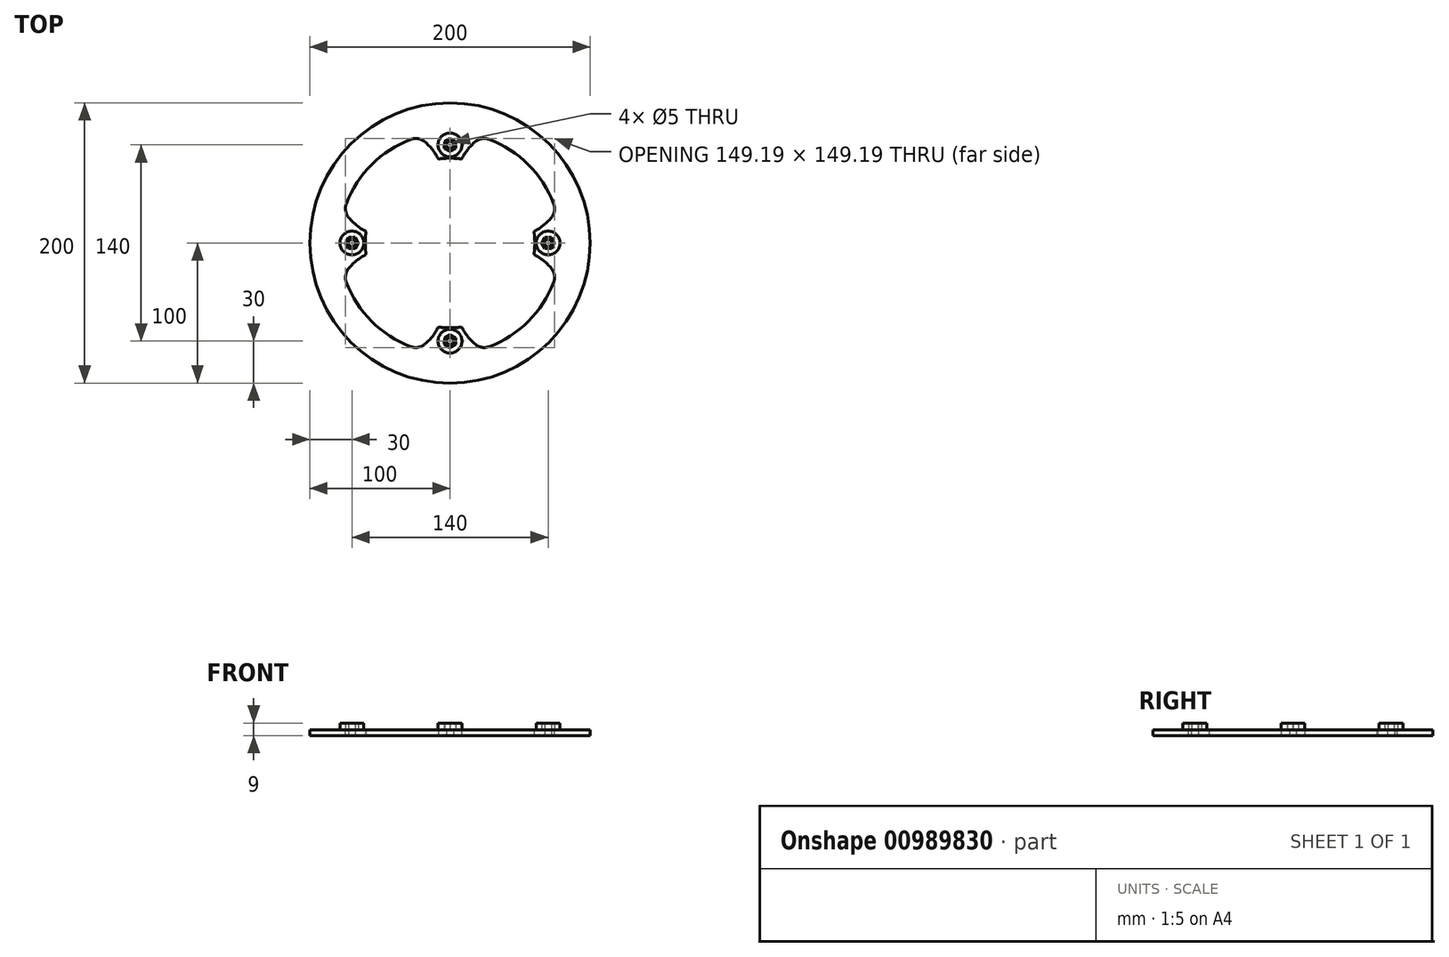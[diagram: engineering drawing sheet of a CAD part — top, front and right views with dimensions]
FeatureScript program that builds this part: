
annotation { "Feature Type Name" : "Feature", "Feature Type Description" : "" }
export const myFeature = defineFeature(function(context is Context, id is Id, definition is map)
    precondition{}
    {
        {
            var Q0;
            Q0=qCreatedBy(makeId("Top.planeOp"),FACE);
            var sketch = newSketch(context, id + "F0", { "sketchPlane" : qUnion([Q0])});
            skCircle(sketch, "E0", {"center": v(0, 0) * mm, "radius": 100 * mm});
            skCircle(sketch, "E1", {"center": v(0, 70) * mm, "radius": 2.5 * mm});
            skCircle(sketch, "E2.1.0", {"center": v(70, 0) * mm, "radius": 2.5 * mm});
            skCircle(sketch, "E2.2.0", {"center": v(0, -70) * mm, "radius": 2.5 * mm});
            skCircle(sketch, "E2.3.0", {"center": v(-70, 0) * mm, "radius": 2.5 * mm});
            skLineSegment(sketch, "E2.anchor1", {"start": v(0, 0) * mm, "end": v(0, 70) * mm, "construction": true});
            skLineSegment(sketch, "E2.anchor2", {"start": v(0, 0) * mm, "end": v(-70, 0) * mm, "construction": true});
            skCircle(sketch, "E3", {"center": v(0, 0) * mm, "radius": 60.5 * mm});
            skLineSegment(sketch, "E4.0", {"start": v(-67.7, -3.72) * mm, "end": v(-72.3, -3.72) * mm});
            skLineSegment(sketch, "E4.1", {"start": v(-72.3, -3.72) * mm, "end": v(-74.62, 0.28) * mm});
            skLineSegment(sketch, "E4.2", {"start": v(-74.62, 0.28) * mm, "end": v(-72.3, 4.28) * mm});
            skLineSegment(sketch, "E4.3", {"start": v(-72.3, 4.28) * mm, "end": v(-67.7, 4.28) * mm});
            skLineSegment(sketch, "E4.4", {"start": v(-67.7, 4.28) * mm, "end": v(-65.38, 0.28) * mm});
            skLineSegment(sketch, "E4.5", {"start": v(-65.38, 0.28) * mm, "end": v(-67.7, -3.72) * mm});
            skPoint(sketch, "E4.0.midPoint", {"position": v(-70, -3.72) * mm});
            skLineSegment(sketch, "E5.1.0", {"start": v(-4.28, -72.3) * mm, "end": v(-4.28, -67.7) * mm});
            skLineSegment(sketch, "E5.1.1", {"start": v(-4.28, -67.7) * mm, "end": v(-0.28, -65.38) * mm});
            skLineSegment(sketch, "E5.1.2", {"start": v(-0.28, -74.62) * mm, "end": v(-4.28, -72.3) * mm});
            skLineSegment(sketch, "E5.1.3", {"start": v(3.72, -72.3) * mm, "end": v(-0.28, -74.62) * mm});
            skLineSegment(sketch, "E5.1.4", {"start": v(3.72, -67.7) * mm, "end": v(3.72, -72.3) * mm});
            skLineSegment(sketch, "E5.1.5", {"start": v(-0.28, -65.38) * mm, "end": v(3.72, -67.7) * mm});
            skLineSegment(sketch, "E5.2.0", {"start": v(72.3, -4.28) * mm, "end": v(67.7, -4.28) * mm});
            skLineSegment(sketch, "E5.2.1", {"start": v(67.7, -4.28) * mm, "end": v(65.38, -0.28) * mm});
            skLineSegment(sketch, "E5.2.2", {"start": v(74.62, -0.28) * mm, "end": v(72.3, -4.28) * mm});
            skLineSegment(sketch, "E5.2.3", {"start": v(72.3, 3.72) * mm, "end": v(74.62, -0.28) * mm});
            skLineSegment(sketch, "E5.2.4", {"start": v(67.7, 3.72) * mm, "end": v(72.3, 3.72) * mm});
            skLineSegment(sketch, "E5.2.5", {"start": v(65.38, -0.28) * mm, "end": v(67.7, 3.72) * mm});
            skLineSegment(sketch, "E5.3.0", {"start": v(4.28, 72.3) * mm, "end": v(4.28, 67.7) * mm});
            skLineSegment(sketch, "E5.3.1", {"start": v(4.28, 67.7) * mm, "end": v(0.28, 65.38) * mm});
            skLineSegment(sketch, "E5.3.2", {"start": v(0.28, 74.62) * mm, "end": v(4.28, 72.3) * mm});
            skLineSegment(sketch, "E5.3.3", {"start": v(-3.72, 72.3) * mm, "end": v(0.28, 74.62) * mm});
            skLineSegment(sketch, "E5.3.4", {"start": v(-3.72, 67.7) * mm, "end": v(-3.72, 72.3) * mm});
            skLineSegment(sketch, "E5.3.5", {"start": v(0.28, 65.38) * mm, "end": v(-3.72, 67.7) * mm});
            skCircle(sketch, "E6", {"center": v(0, 0) * mm, "radius": 79.07 * mm});
            skArc(sketch, "E7", {"start": v(-75.7, 22.83) * mm, "mid": v(-68.85, 14.45) * mm, "end": v(-59.93, 8.3) * mm});
            skArc(sketch, "E8.1.0", {"start": v(-22.83, -75.7) * mm, "mid": v(-14.45, -68.85) * mm, "end": v(-8.3, -59.93) * mm});
            skArc(sketch, "E8.2.0", {"start": v(75.7, -22.83) * mm, "mid": v(68.85, -14.45) * mm, "end": v(59.93, -8.3) * mm});
            skArc(sketch, "E8.3.0", {"start": v(22.83, 75.7) * mm, "mid": v(14.45, 68.85) * mm, "end": v(8.3, 59.93) * mm});
            skArc(sketch, "E9.trimOffspring", {"start": v(-8.3, 59.93) * mm, "mid": v(-14.45, 68.85) * mm, "end": v(-22.83, 75.7) * mm});
            skArc(sketch, "E10.trimOffspring", {"start": v(59.93, 8.3) * mm, "mid": v(68.85, 14.45) * mm, "end": v(75.7, 22.83) * mm});
            skArc(sketch, "E11.trimOffspring", {"start": v(8.3, -59.93) * mm, "mid": v(14.45, -68.85) * mm, "end": v(22.83, -75.7) * mm});
            skArc(sketch, "E12.trimOffspring", {"start": v(-59.93, -8.3) * mm, "mid": v(-68.85, -14.45) * mm, "end": v(-75.7, -22.83) * mm});
            skSolve(sketch);
        }
        {
            var Q0;
            Q0=makeQuery(id+"F0.imprint","IMPRINT",FACE,{"disambiguationData":[TD([[makeQuery(id+"F0.imprint","IMPRINT",EDGE,{"derivedFrom":sQuery(id+"F0.wireOp",EDGE,"E0")}),1.0]])]});
            var Q1;
            Q1=makeQuery(id+"F0.imprint","IMPRINT",FACE,{"disambiguationData":[TD([[makeQuery(id+"F0.imprint","IMPRINT",EDGE,{"derivedFrom":sQuery(id+"F0.wireOp",EDGE,"E2.3.0")}),-1.0]])]});
            var Q2;
            Q2=makeQuery(id+"F0.imprint","IMPRINT",FACE,{"disambiguationData":[TD([[makeQuery(id+"F0.imprint","IMPRINT",EDGE,{"derivedFrom":sQuery(id+"F0.wireOp",EDGE,"E2.2.0")}),-1.0]])]});
            var Q3;
            Q3=makeQuery(id+"F0.imprint","IMPRINT",FACE,{"disambiguationData":[TD([[makeQuery(id+"F0.imprint","IMPRINT",EDGE,{"derivedFrom":sQuery(id+"F0.wireOp",EDGE,"E2.1.0")}),-1.0]])]});
            var Q4;
            Q4=makeQuery(id+"F0.imprint","IMPRINT",FACE,{"disambiguationData":[TD([[makeQuery(id+"F0.imprint","IMPRINT",EDGE,{"derivedFrom":sQuery(id+"F0.wireOp",EDGE,"E1")}),-1.0]])]});
            var Q5;
            Q5=makeQuery(id+"F0.imprint","IMPRINT",FACE,{"disambiguationData":[TD([[makeQuery(id+"F0.imprint","IMPRINT",EDGE,{"derivedFrom":sQuery(id+"F0.wireOp",EDGE,"E5.3.0")}),1.0]])]});
            var Q6;
            Q6=makeQuery(id+"F0.imprint","IMPRINT",FACE,{"disambiguationData":[TD([[makeQuery(id+"F0.imprint","IMPRINT",EDGE,{"derivedFrom":sQuery(id+"F0.wireOp",EDGE,"E4.0")}),1.0]])]});
            var Q7;
            Q7=makeQuery(id+"F0.imprint","IMPRINT",FACE,{"disambiguationData":[TD([[makeQuery(id+"F0.imprint","IMPRINT",EDGE,{"derivedFrom":sQuery(id+"F0.wireOp",EDGE,"E5.2.0")}),1.0]])]});
            var Q8;
            Q8=makeQuery(id+"F0.imprint","IMPRINT",FACE,{"disambiguationData":[TD([[makeQuery(id+"F0.imprint","IMPRINT",EDGE,{"derivedFrom":sQuery(id+"F0.wireOp",EDGE,"E5.1.0")}),1.0]])]});
            extrude(context, id + "F1", {"entities" : qUnion([Q0, Q1, Q2, Q3, Q4, Q5, Q6, Q7, Q8]), "depth" : 4 * mm, "offsetDistance" : 25 * mm});
        }
        {
            var Q0;
            Q0=makeQuery(id+"F1.opExtrude","CAP_FACE",FACE,{"disambiguationData":[OSD([sQuery(id+"F0.wireOp",EDGE,"E0"),sQuery(id+"F0.wireOp",EDGE,"E1"),sQuery(id+"F0.wireOp",EDGE,"E2.1.0"),sQuery(id+"F0.wireOp",EDGE,"E2.2.0"),sQuery(id+"F0.wireOp",EDGE,"E2.3.0"),sQuery(id+"F0.wireOp",EDGE,"E3")])],"isStart":false});
            var sketch = newSketch(context, id + "F2", { "sketchPlane" : qUnion([Q0])});
            skCircle(sketch, "E13", {"center": v(-70, 0) * mm, "radius": 8.5 * mm});
            skCircle(sketch, "E14", {"center": v(0, 70) * mm, "radius": 8.5 * mm});
            skCircle(sketch, "E15", {"center": v(70, 0) * mm, "radius": 8.5 * mm});
            skCircle(sketch, "E16", {"center": v(0, -70) * mm, "radius": 8.5 * mm});
            skCircle(sketch, "E17.cCircle", {"center": v(-70, 0) * mm, "radius": 4 * mm, "construction": true});
            skLineSegment(sketch, "E17.0", {"start": v(-72.36, -3.97) * mm, "end": v(-74.62, 0.05) * mm});
            skLineSegment(sketch, "E17.1", {"start": v(-74.62, 0.05) * mm, "end": v(-72.26, 4.03) * mm});
            skLineSegment(sketch, "E17.2", {"start": v(-72.26, 4.03) * mm, "end": v(-67.64, 3.97) * mm});
            skLineSegment(sketch, "E17.3", {"start": v(-67.64, 3.97) * mm, "end": v(-65.38, -0.05) * mm});
            skLineSegment(sketch, "E17.4", {"start": v(-65.38, -0.05) * mm, "end": v(-67.74, -4.03) * mm});
            skLineSegment(sketch, "E17.5", {"start": v(-67.74, -4.03) * mm, "end": v(-72.36, -3.97) * mm});
            skPoint(sketch, "E17.0.midPoint", {"position": v(-73.49, -1.96) * mm});
            skLineSegment(sketch, "E18.1.0", {"start": v(3.97, -72.36) * mm, "end": v(-0.05, -74.62) * mm});
            skLineSegment(sketch, "E18.1.1", {"start": v(-3.97, -67.64) * mm, "end": v(0.05, -65.38) * mm});
            skLineSegment(sketch, "E18.1.2", {"start": v(-4.03, -72.26) * mm, "end": v(-3.97, -67.64) * mm});
            skPoint(sketch, "E18.1.3", {"position": v(1.96, -73.49) * mm});
            skLineSegment(sketch, "E18.1.4", {"start": v(0.05, -65.38) * mm, "end": v(4.03, -67.74) * mm});
            skLineSegment(sketch, "E18.1.5", {"start": v(-0.05, -74.62) * mm, "end": v(-4.03, -72.26) * mm});
            skCircle(sketch, "E18.1.6", {"center": v(0, -70) * mm, "radius": 4 * mm, "construction": true});
            skLineSegment(sketch, "E18.1.7", {"start": v(4.03, -67.74) * mm, "end": v(3.97, -72.36) * mm});
            skLineSegment(sketch, "E18.2.0", {"start": v(72.36, 3.97) * mm, "end": v(74.62, -0.05) * mm});
            skLineSegment(sketch, "E18.2.1", {"start": v(67.64, -3.97) * mm, "end": v(65.38, 0.05) * mm});
            skLineSegment(sketch, "E18.2.2", {"start": v(72.26, -4.03) * mm, "end": v(67.64, -3.97) * mm});
            skPoint(sketch, "E18.2.3", {"position": v(73.49, 1.96) * mm});
            skLineSegment(sketch, "E18.2.4", {"start": v(65.38, 0.05) * mm, "end": v(67.74, 4.03) * mm});
            skLineSegment(sketch, "E18.2.5", {"start": v(74.62, -0.05) * mm, "end": v(72.26, -4.03) * mm});
            skCircle(sketch, "E18.2.6", {"center": v(70, 0) * mm, "radius": 4 * mm, "construction": true});
            skLineSegment(sketch, "E18.2.7", {"start": v(67.74, 4.03) * mm, "end": v(72.36, 3.97) * mm});
            skLineSegment(sketch, "E18.3.0", {"start": v(-3.97, 72.36) * mm, "end": v(0.05, 74.62) * mm});
            skLineSegment(sketch, "E18.3.1", {"start": v(3.97, 67.64) * mm, "end": v(-0.05, 65.38) * mm});
            skLineSegment(sketch, "E18.3.2", {"start": v(4.03, 72.26) * mm, "end": v(3.97, 67.64) * mm});
            skPoint(sketch, "E18.3.3", {"position": v(-1.96, 73.49) * mm});
            skLineSegment(sketch, "E18.3.4", {"start": v(-0.05, 65.38) * mm, "end": v(-4.03, 67.74) * mm});
            skLineSegment(sketch, "E18.3.5", {"start": v(0.05, 74.62) * mm, "end": v(4.03, 72.26) * mm});
            skCircle(sketch, "E18.3.6", {"center": v(0, 70) * mm, "radius": 4 * mm, "construction": true});
            skLineSegment(sketch, "E18.3.7", {"start": v(-4.03, 67.74) * mm, "end": v(-3.97, 72.36) * mm});
            skPoint(sketch, "E18.center", {"position": v(0, 0) * mm});
            skSolve(sketch);
        }
        {
            var Q0;
            Q0=makeQuery(id+"F2.imprint","IMPRINT",FACE,{"disambiguationData":[TD([[makeQuery(id+"F2.imprint","IMPRINT",EDGE,{"derivedFrom":sQuery(id+"F2.wireOp",EDGE,"E13")}),1.0]])]});
            var Q1;
            Q1=makeQuery(id+"F2.imprint","IMPRINT",FACE,{"disambiguationData":[TD([[makeQuery(id+"F2.imprint","IMPRINT",EDGE,{"derivedFrom":sQuery(id+"F2.wireOp",EDGE,"E14")}),1.0]])]});
            var Q2;
            Q2=makeQuery(id+"F2.imprint","IMPRINT",FACE,{"disambiguationData":[TD([[makeQuery(id+"F2.imprint","IMPRINT",EDGE,{"derivedFrom":sQuery(id+"F2.wireOp",EDGE,"E15")}),1.0]])]});
            var Q3;
            Q3=makeQuery(id+"F2.imprint","IMPRINT",FACE,{"disambiguationData":[TD([[makeQuery(id+"F2.imprint","IMPRINT",EDGE,{"derivedFrom":sQuery(id+"F2.wireOp",EDGE,"E16")}),1.0]])]});
            extrude(context, id + "F3", {"entities" : qUnion([Q0, Q1, Q2, Q3]), "operationType" : NewBodyOperationType.ADD, "depth" : 5 * mm, "offsetDistance" : 25 * mm});
        }
        {
            var Q0;
            Q0=makeQuery(id+"F1.opExtrude","SWEPT_EDGE",EDGE,{"disambiguationData":[OSD([sQuery(id+"F0.wireOp",EDGE,"E6"),sQuery(id+"F0.wireOp",EDGE,"E7")])]});
            var Q1;
            Q1=makeQuery(id+"F1.opExtrude","SWEPT_EDGE",EDGE,{"disambiguationData":[OSD([sQuery(id+"F0.wireOp",EDGE,"E6"),sQuery(id+"F0.wireOp",EDGE,"E12.trimOffspring")])]});
            var Q2;
            Q2=makeQuery(id+"F1.opExtrude","SWEPT_EDGE",EDGE,{"disambiguationData":[OSD([sQuery(id+"F0.wireOp",EDGE,"E6"),sQuery(id+"F0.wireOp",EDGE,"E8.2.0")])]});
            var Q3;
            Q3=makeQuery(id+"F1.opExtrude","SWEPT_EDGE",EDGE,{"disambiguationData":[OSD([sQuery(id+"F0.wireOp",EDGE,"E6"),sQuery(id+"F0.wireOp",EDGE,"E11.trimOffspring")])]});
            var Q4;
            Q4=makeQuery(id+"F1.opExtrude","SWEPT_EDGE",EDGE,{"disambiguationData":[OSD([sQuery(id+"F0.wireOp",EDGE,"E6"),sQuery(id+"F0.wireOp",EDGE,"E8.1.0")])]});
            var Q5;
            Q5=makeQuery(id+"F1.opExtrude","SWEPT_EDGE",EDGE,{"disambiguationData":[OSD([sQuery(id+"F0.wireOp",EDGE,"E6"),sQuery(id+"F0.wireOp",EDGE,"E10.trimOffspring")])]});
            var Q6;
            Q6=makeQuery(id+"F1.opExtrude","SWEPT_EDGE",EDGE,{"disambiguationData":[OSD([sQuery(id+"F0.wireOp",EDGE,"E6"),sQuery(id+"F0.wireOp",EDGE,"E8.3.0")])]});
            var Q7;
            Q7=makeQuery(id+"F1.opExtrude","SWEPT_EDGE",EDGE,{"disambiguationData":[OSD([sQuery(id+"F0.wireOp",EDGE,"E6"),sQuery(id+"F0.wireOp",EDGE,"E9.trimOffspring")])]});
            fillet(context, id + "F4", {"entities" : qUnion([Q0, Q1, Q2, Q3, Q4, Q5, Q6, Q7]), "radius" : 10 * mm, "tangentPropagation" : true, "allowEdgeOverflow" : false});
        }
        {
            var Q0;
            Q0=makeQuery(id+"F3.opExtrude","CAP_EDGE",EDGE,{"disambiguationData":[OSD([sQuery(id+"F2.wireOp",EDGE,"E16")])],"isStart":true});
            var Q1;
            Q1=makeQuery(id+"F3.opExtrude","CAP_EDGE",EDGE,{"disambiguationData":[OSD([sQuery(id+"F2.wireOp",EDGE,"E14")])],"isStart":true});
            var Q2;
            Q2=makeQuery(id+"F3.opExtrude","CAP_EDGE",EDGE,{"disambiguationData":[OSD([sQuery(id+"F2.wireOp",EDGE,"E13")])],"isStart":true});
            var Q3;
            Q3=makeQuery(id+"F3.opExtrude","CAP_EDGE",EDGE,{"disambiguationData":[OSD([sQuery(id+"F2.wireOp",EDGE,"E15")])],"isStart":true});
            fillet(context, id + "F5", {"entities" : qUnion([Q0, Q1, Q2, Q3]), "radius" : 1 * mm, "tangentPropagation" : true, "allowEdgeOverflow" : false});
        }
    });
